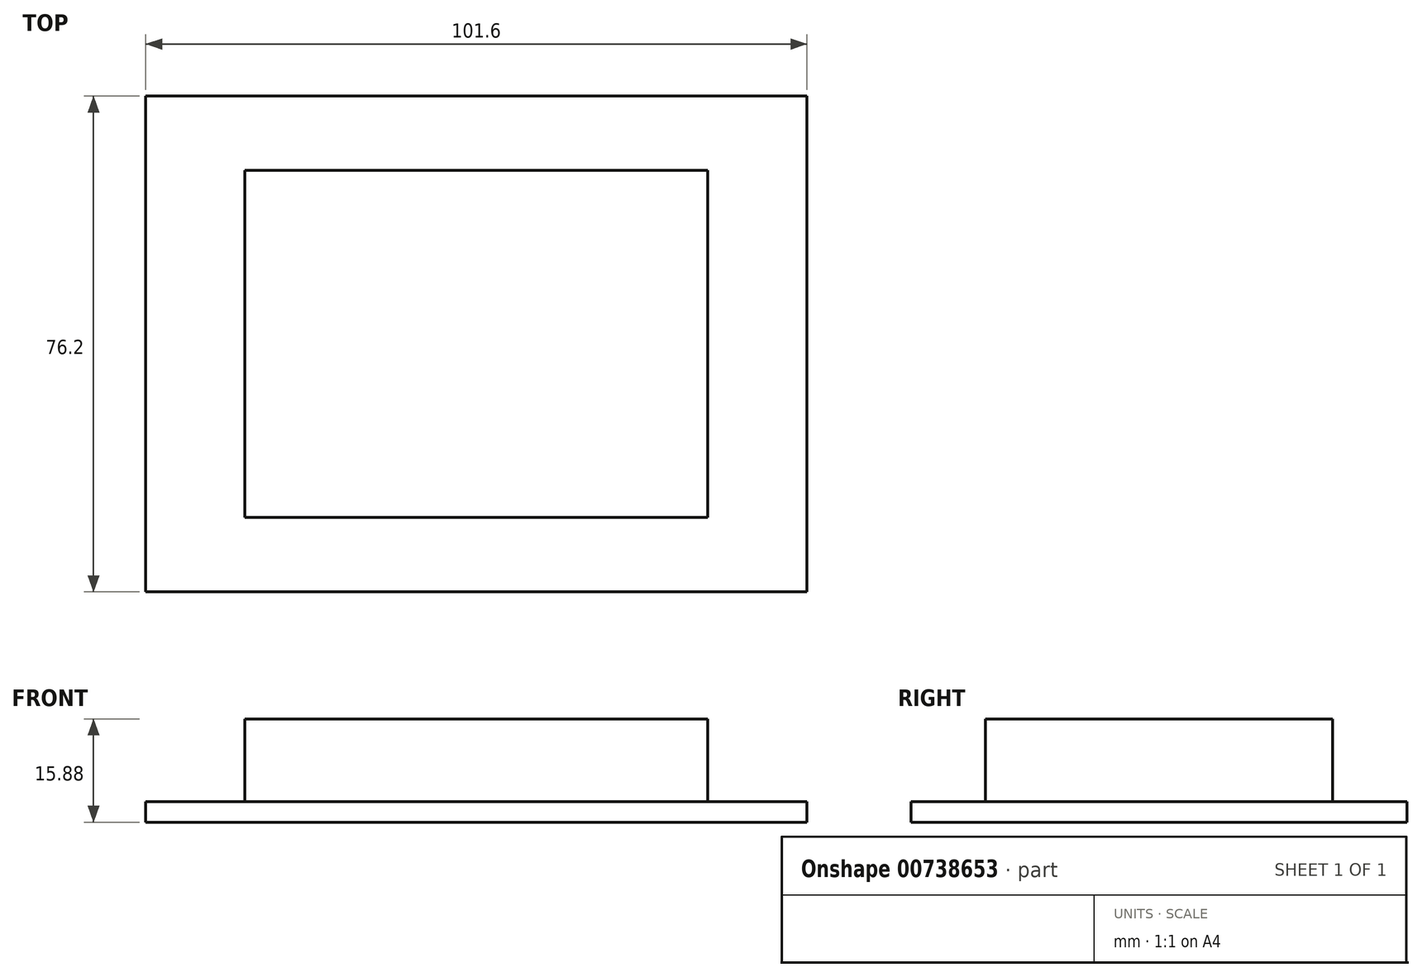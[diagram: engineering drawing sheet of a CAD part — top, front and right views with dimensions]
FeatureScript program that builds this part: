
annotation { "Feature Type Name" : "Feature", "Feature Type Description" : "" }
export const myFeature = defineFeature(function(context is Context, id is Id, definition is map)
    precondition{}
    {
        {
            var Q0;
            Q0=qCreatedBy(makeId("Top.planeOp"),FACE);
            var sketch = newSketch(context, id + "F0", { "sketchPlane" : qUnion([Q0])});
            skLineSegment(sketch, "E0.bottom", {"start": v(50.8, -38.1) * mm, "end": v(-50.8, -38.1) * mm});
            skLineSegment(sketch, "E0.top", {"start": v(50.8, 38.1) * mm, "end": v(-50.8, 38.1) * mm});
            skLineSegment(sketch, "E0.left", {"start": v(50.8, -38.1) * mm, "end": v(50.8, 38.1) * mm});
            skLineSegment(sketch, "E0.right", {"start": v(-50.8, -38.1) * mm, "end": v(-50.8, 38.1) * mm});
            skPoint(sketch, "E0.middle", {"position": v(0, 0) * mm});
            skLineSegment(sketch, "E1.bottom", {"start": v(35.56, -26.67) * mm, "end": v(-35.56, -26.67) * mm});
            skLineSegment(sketch, "E1.top", {"start": v(35.56, 26.67) * mm, "end": v(-35.56, 26.67) * mm});
            skLineSegment(sketch, "E1.left", {"start": v(35.56, -26.67) * mm, "end": v(35.56, 26.67) * mm});
            skLineSegment(sketch, "E1.right", {"start": v(-35.56, -26.67) * mm, "end": v(-35.56, 26.67) * mm});
            skSolve(sketch);
        }
        {
            var Q0;
            Q0=makeQuery(id+"F0.imprint","IMPRINT",FACE,{"disambiguationData":[TD([[makeQuery(id+"F0.imprint","IMPRINT",EDGE,{"derivedFrom":sQuery(id+"F0.wireOp",EDGE,"E1.bottom")}),-1.0]])]});
            var Q1;
            Q1=makeQuery(id+"F0.imprint","IMPRINT",FACE,{"disambiguationData":[TD([[makeQuery(id+"F0.imprint","IMPRINT",EDGE,{"derivedFrom":sQuery(id+"F0.wireOp",EDGE,"E0.bottom")}),-1.0]])]});
            extrude(context, id + "F1", {"entities" : qUnion([Q0, Q1]), "depth" : 3.17 * mm, "offsetDistance" : 25.4 * mm});
        }
        {
            var Q0;
            Q0=makeQuery(id+"F0.imprint","IMPRINT",FACE,{"disambiguationData":[TD([[makeQuery(id+"F0.imprint","IMPRINT",EDGE,{"derivedFrom":sQuery(id+"F0.wireOp",EDGE,"E1.bottom")}),-1.0]])]});
            extrude(context, id + "F2", {"entities" : qUnion([Q0]), "operationType" : NewBodyOperationType.ADD, "depth" : 15.88 * mm, "offsetDistance" : 25.4 * mm});
        }
    });
